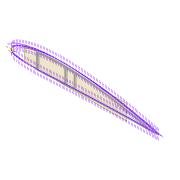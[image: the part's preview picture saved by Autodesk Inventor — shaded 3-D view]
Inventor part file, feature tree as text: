
AUTODESK INVENTOR PART (.ipt)
format: ipt  version: 2022 (Build 260153000, 153)  size: 364,544 bytes
history: native  units: mm
features: extrude x7, sketch x7, projected_geometry x5, shell x1, fillet x1, plane x1
ambient origin geometry x8: Origin, YZ Plane, XZ Plane, XY Plane, X Axis, Y Axis, Z Axis, Center Point
bodies: Solid1 (feature_tree)
feature tree (22):
  extrude  "Extrusion1"  Depth=5.0mm
  shell  "Shell1"  Thickness=2.0mm
  extrude  "Extrusion8"  Depth=5.9mm
  extrude  "Extrusion3"  Depth=10.0mm TaperAngle=0.0deg
  extrude  "Extrusion4"  Depth=2.0mm
  fillet  "Fillet1"  Radius=5.0mm
  extrude  "Extrusion5"  Depth=2.5mm
  plane  "Work Plane2"
  extrude  "Extrusion9"  Depth=1.6mm
  extrude  "Extrusion10"  Depth=0.5mm
  sketch  "Sketch3"  dims[d0=4.0mm d1=0.0mm d2=5.0mm d7=2.0mm]
  sketch  "Sketch8"  dims[d8=2.0mm d9=5.9mm]
  sketch  "Sketch9"  dims[d13=10.0mm d14=0.0mm d16=10.0mm d17=0.0mm]
  sketch  "Sketch10"  dims[d22=4.0mm d23=0.0mm d31=2.0mm d32=5.0mm]
  projected_geometry  "Projected Loop4"
  projected_geometry  "Projected Loop10"
  sketch  "Sketch24"  dims[d34=1.6mm d35=2.5mm]
  projected_geometry  "Projected Loop11"
  projected_geometry  "Projected Loop12"
  sketch  "Sketch26"  dims[d37=5.0mm d38=1.6mm]
  projected_geometry  "Projected Loop13"
  sketch  "Sketch27"  dims[d40=2.5mm d62=72.0mm d63=6.0mm d64=4.0mm d65=0.0mm d66=3.0mm d67=12.0mm d68=75.0mm d69=20.0mm d70=0.5mm d71=10.0mm d72=0.0mm d73=10.0mm d74=0.0mm]
